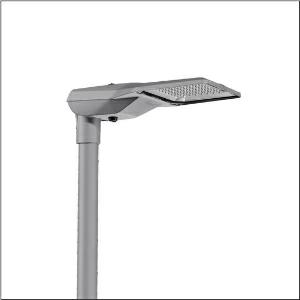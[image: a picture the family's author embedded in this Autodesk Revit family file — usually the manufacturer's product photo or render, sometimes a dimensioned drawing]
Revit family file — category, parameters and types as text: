
# Revit family: streetlight_sl_21_midi___st0_8a_5xe3c33t08nb_d41b
name_source: partatom
category: Lighting Fixtures
units: mm (PartAtom-declared; Revit-internal decimal feet)

## family parameters
Cut with Voids When Loaded = No
Host = Face
Light Source = No
Part Type = Normal
Room Calculation Point = No
Round Connector Dimension = Use Diameter
Shared = No

## types (1)
- --- (1 x LED, 22700 lm, 151.2 W, 3000K)
    Apparent Load = 151 VA
    CIE Flux Codes = 41 75 97 100 100
    Color Rendering = 70
    Color Temperature = 3000K
    Default Elevation = 1800 mm
    Description = Streetlight SL 21 midi, mast luminaire, primary light control with lens, of PMMA, primary optical cover: cover, of toughened safety glass, transparent, light distribution: ST0.8a, light emission: direct distribution, primary light characteristic: asymmetric, installation type: side-entry, post-top, LED, High Power LED, rated luminous flux: 22.700lm, luminous efficacy: 150lm/W, light colour: 730, colour temperature: 3000K, control: overheat protection, constant luminous flux control, time-dependent luminous flux control, flexible luminous flux parameterisation, presetting dimming logarithmic, mains connection: 230..240V, AC, 50/60Hz, start of lifetime: 151W, end of service life: 157W, reduction: 70W, luminaire housing, of diecast aluminium, powder-coated, Siteco® metallic grey (DB 702S), corrosivity category C5 mid according to DIN EN ISO 12944, please order mast flange separately, inclination adjustable: 0°, 5°, 10°, 15°, sealing non-destructively replaceable, multi-level sealing system, length: 644mm, width: 335mm, height: 110mm, mast flange for spigot size: 42mm (side-entry): 5XC10008XM4, 60/48mm (side-entry/post-top): 5XC10108XM2, 76/60mm (side-entry/post-top): 5XC10108XM1, Smart Interface below and above, protection rating (complete): IP66, insulation class (complete): insulation class II (safety insulation), certification: CE, ENEC, ENEC+, VDE, impact resistance: IK09, permissible operating ambient temperature for outdoor applications: -40..+50°C, standard-compliant lighting for roads and squares, packaging unit: 1 piece

Light Distribution: ST0.8a
    Height = 111 mm
    Lamp = 1 x LED
    Lamp Light Flux = 22700 lm
    Lamp Power = 151.2 W
    Lamp count = 1
    Length = 644 mm
    Luminous efficacy = 150 lm/W
    Manufacturer = Siteco
    ModVariant = No
    Model = 5XE3C33T08NB
    Number of Poles = 1
    OnlyDefault = Yes
    Power Factor = 1
    Product Name = Streetlight SL 21 midi | ST0.8a
    Product group = mast luminaire | pylon top
    ProductGroupID = 6100
    Protection Class = Protection class II
    Protection Degree = IP 66
    RLX_Detail_Level = 1
    RLX_Emergency_Light_Flux = 0 lm
    RLX_Emergency_Type = 0
    RLX_Emergency_Type_DB = No
    RlxData = <blob elided: 90785 chars, md5=96c3ee6f>
    Socket = socket
    Standby Power = 0 W
    System Light Flux = 22700 lm
    System Power = 151 W
    Type Comments = factory setting: luminous flux: 100 % | dim-lin: 254 | 802 mA
    Type Image = l_1004304.jpg
    URL = http://relux.com
    VarID = @adj_118925
    Voltage = 0 V
    Weight = 0.00 kg
    Width = 336 mm

## geometry (parser evidence)
native form markers: Blend x4, Sweep x11
no freeform markers — native parametric forms only
